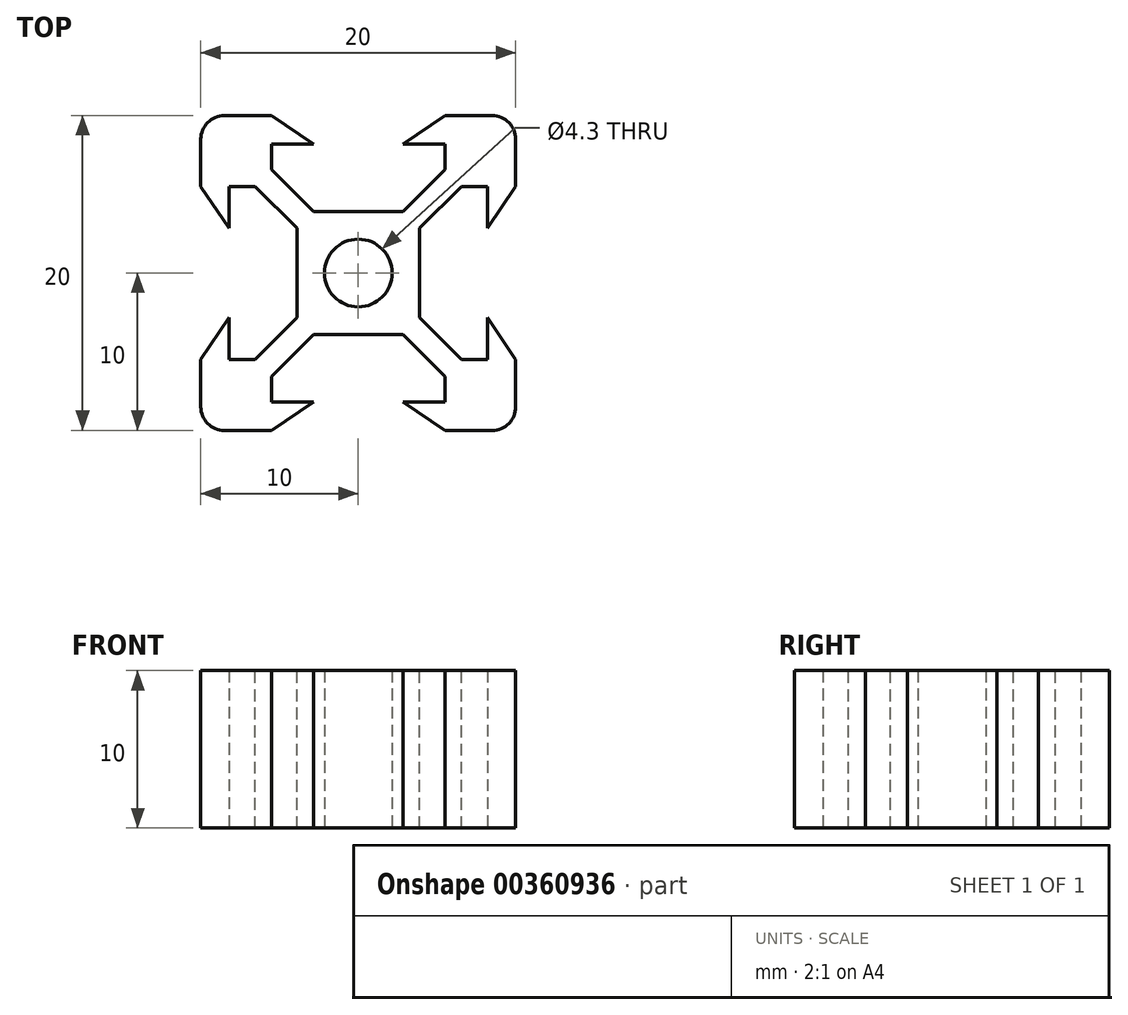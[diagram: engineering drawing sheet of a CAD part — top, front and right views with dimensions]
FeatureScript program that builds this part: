
annotation { "Feature Type Name" : "Feature", "Feature Type Description" : "" }
export const myFeature = defineFeature(function(context is Context, id is Id, definition is map)
    precondition{}
    {
        {
            var Q0;
            Q0=qCreatedBy(makeId("Top.planeOp"),FACE);
            var sketch = newSketch(context, id + "F0", { "sketchPlane" : qUnion([Q0])});
            skPoint(sketch, "E0.middle", {"position": v(0, 0) * mm});
            skPoint(sketch, "E1.visualSharp", {"position": v(-10, 10) * mm});
            skArc(sketch, "E1.filletArc", {"start": v(-8.5, 10) * mm, "mid": v(-9.56, 9.56) * mm, "end": v(-10, 8.5) * mm});
            skPoint(sketch, "E2.visualSharp", {"position": v(10, 10) * mm});
            skArc(sketch, "E2.filletArc", {"start": v(10, 8.5) * mm, "mid": v(9.56, 9.56) * mm, "end": v(8.5, 10) * mm});
            skPoint(sketch, "E3.visualSharp", {"position": v(10, -10) * mm});
            skArc(sketch, "E3.filletArc", {"start": v(8.5, -10) * mm, "mid": v(9.56, -9.56) * mm, "end": v(10, -8.5) * mm});
            skPoint(sketch, "E4.visualSharp", {"position": v(-10, -10) * mm});
            skArc(sketch, "E4.filletArc", {"start": v(-10, -8.5) * mm, "mid": v(-9.56, -9.56) * mm, "end": v(-8.5, -10) * mm});
            skLineSegment(sketch, "E5", {"start": v(-10, 5.5) * mm, "end": v(-8.2, 2.84) * mm});
            skLineSegment(sketch, "E6", {"start": v(-8.2, -2.84) * mm, "end": v(-10, -5.5) * mm});
            skLineSegment(sketch, "E7.1.0", {"start": v(-5.5, -10) * mm, "end": v(-2.84, -8.2) * mm});
            skLineSegment(sketch, "E7.1.2", {"start": v(2.84, -8.2) * mm, "end": v(5.5, -10) * mm});
            skLineSegment(sketch, "E7.2.0", {"start": v(10, -5.5) * mm, "end": v(8.2, -2.84) * mm});
            skLineSegment(sketch, "E7.2.2", {"start": v(8.2, 2.84) * mm, "end": v(10, 5.5) * mm});
            skLineSegment(sketch, "E7.3.0", {"start": v(5.5, 10) * mm, "end": v(2.84, 8.2) * mm});
            skLineSegment(sketch, "E7.3.2", {"start": v(-2.84, 8.2) * mm, "end": v(-5.5, 10) * mm});
            skLineSegment(sketch, "E8", {"start": v(-10, 5.5) * mm, "end": v(-10, 8.5) * mm});
            skLineSegment(sketch, "E9", {"start": v(-8.5, 10) * mm, "end": v(-5.5, 10) * mm});
            skLineSegment(sketch, "E10", {"start": v(5.5, 10) * mm, "end": v(8.5, 10) * mm});
            skLineSegment(sketch, "E11", {"start": v(10, 8.5) * mm, "end": v(10, 5.5) * mm});
            skLineSegment(sketch, "E12", {"start": v(10, -5.5) * mm, "end": v(10, -8.5) * mm});
            skLineSegment(sketch, "E13", {"start": v(5.5, -10) * mm, "end": v(8.5, -10) * mm});
            skLineSegment(sketch, "E14", {"start": v(-5.5, -10) * mm, "end": v(-8.5, -10) * mm});
            skLineSegment(sketch, "E15", {"start": v(-10, -8.5) * mm, "end": v(-10, -5.5) * mm});
            skCircle(sketch, "E16", {"center": v(0, 0) * mm, "radius": 2.15 * mm});
            skLineSegment(sketch, "E17", {"start": v(-8.2, 2.84) * mm, "end": v(-8.2, -2.84) * mm});
            skLineSegment(sketch, "E18", {"start": v(-2.84, -8.2) * mm, "end": v(2.84, -8.2) * mm});
            skLineSegment(sketch, "E19", {"start": v(8.2, -2.84) * mm, "end": v(8.2, 2.84) * mm});
            skLineSegment(sketch, "E20", {"start": v(2.84, 8.2) * mm, "end": v(-2.84, 8.2) * mm});
            skSolve(sketch);
        }
        {
            var Q0;
            Q0=qSketchRegion(id+"F0",true);
            extrude(context, id + "F1", {"entities" : qUnion([Q0]), "depth" : 10 * mm});
        }
        {
            var Q0;
            Q0=makeQuery(id+"F1.opExtrude","CAP_FACE",FACE,{"disambiguationData":[OSD([sQuery(id+"F0.wireOp",EDGE,"E1.filletArc"),sQuery(id+"F0.wireOp",EDGE,"E2.filletArc"),sQuery(id+"F0.wireOp",EDGE,"E3.filletArc"),sQuery(id+"F0.wireOp",EDGE,"E4.filletArc"),sQuery(id+"F0.wireOp",EDGE,"E5"),sQuery(id+"F0.wireOp",EDGE,"E6"),sQuery(id+"F0.wireOp",EDGE,"E7.1.0"),sQuery(id+"F0.wireOp",EDGE,"E7.1.2"),sQuery(id+"F0.wireOp",EDGE,"E7.2.0"),sQuery(id+"F0.wireOp",EDGE,"E7.2.2"),sQuery(id+"F0.wireOp",EDGE,"E7.3.0"),sQuery(id+"F0.wireOp",EDGE,"E7.3.2"),sQuery(id+"F0.wireOp",EDGE,"E8"),sQuery(id+"F0.wireOp",EDGE,"E9"),sQuery(id+"F0.wireOp",EDGE,"E10"),sQuery(id+"F0.wireOp",EDGE,"E11"),sQuery(id+"F0.wireOp",EDGE,"E12"),sQuery(id+"F0.wireOp",EDGE,"E13"),sQuery(id+"F0.wireOp",EDGE,"E14"),sQuery(id+"F0.wireOp",EDGE,"E15"),sQuery(id+"F0.wireOp",EDGE,"E16"),sQuery(id+"F0.wireOp",EDGE,"E17"),sQuery(id+"F0.wireOp",EDGE,"E18"),sQuery(id+"F0.wireOp",EDGE,"E19"),sQuery(id+"F0.wireOp",EDGE,"E20")])],"isStart":false});
            var sketch = newSketch(context, id + "F2", { "sketchPlane" : qUnion([Q0])});
            skLineSegment(sketch, "E21", {"start": v(-8.2, 2.84) * mm, "end": v(-8.2, 5.5) * mm});
            skLineSegment(sketch, "E22", {"start": v(-8.2, 5.5) * mm, "end": v(-6.56, 5.5) * mm});
            skLineSegment(sketch, "E23", {"start": v(-6.56, 5.5) * mm, "end": v(-3.9, 2.84) * mm});
            skLineSegment(sketch, "E24", {"start": v(-8.2, -2.84) * mm, "end": v(-8.2, -5.5) * mm});
            skLineSegment(sketch, "E25", {"start": v(-8.2, -5.5) * mm, "end": v(-6.56, -5.5) * mm});
            skLineSegment(sketch, "E26", {"start": v(-6.56, -5.5) * mm, "end": v(-3.9, -2.84) * mm});
            skLineSegment(sketch, "E27", {"start": v(-3.9, -2.84) * mm, "end": v(-3.9, 2.84) * mm});
            skLineSegment(sketch, "E28", {"start": v(-8.2, 2.84) * mm, "end": v(-8.2, -2.84) * mm});
            skLineSegment(sketch, "E29.1.0", {"start": v(-2.84, -8.2) * mm, "end": v(2.84, -8.2) * mm});
            skLineSegment(sketch, "E29.1.1", {"start": v(-2.84, -8.2) * mm, "end": v(-5.5, -8.2) * mm});
            skLineSegment(sketch, "E29.1.2", {"start": v(-5.5, -8.2) * mm, "end": v(-5.5, -6.56) * mm});
            skLineSegment(sketch, "E29.1.3", {"start": v(5.5, -8.2) * mm, "end": v(5.5, -6.56) * mm});
            skLineSegment(sketch, "E29.1.4", {"start": v(2.84, -8.2) * mm, "end": v(5.5, -8.2) * mm});
            skLineSegment(sketch, "E29.1.5", {"start": v(2.84, -3.9) * mm, "end": v(-2.84, -3.9) * mm});
            skLineSegment(sketch, "E29.1.6", {"start": v(5.5, -6.56) * mm, "end": v(2.84, -3.9) * mm});
            skLineSegment(sketch, "E29.1.7", {"start": v(-5.5, -6.56) * mm, "end": v(-2.84, -3.9) * mm});
            skLineSegment(sketch, "E29.2.0", {"start": v(8.2, -2.84) * mm, "end": v(8.2, 2.84) * mm});
            skLineSegment(sketch, "E29.2.1", {"start": v(8.2, -2.84) * mm, "end": v(8.2, -5.5) * mm});
            skLineSegment(sketch, "E29.2.2", {"start": v(8.2, -5.5) * mm, "end": v(6.56, -5.5) * mm});
            skLineSegment(sketch, "E29.2.3", {"start": v(8.2, 5.5) * mm, "end": v(6.56, 5.5) * mm});
            skLineSegment(sketch, "E29.2.4", {"start": v(8.2, 2.84) * mm, "end": v(8.2, 5.5) * mm});
            skLineSegment(sketch, "E29.2.5", {"start": v(3.9, 2.84) * mm, "end": v(3.9, -2.84) * mm});
            skLineSegment(sketch, "E29.2.6", {"start": v(6.56, 5.5) * mm, "end": v(3.9, 2.84) * mm});
            skLineSegment(sketch, "E29.2.7", {"start": v(6.56, -5.5) * mm, "end": v(3.9, -2.84) * mm});
            skLineSegment(sketch, "E29.3.0", {"start": v(2.84, 8.2) * mm, "end": v(-2.84, 8.2) * mm});
            skLineSegment(sketch, "E29.3.1", {"start": v(2.84, 8.2) * mm, "end": v(5.5, 8.2) * mm});
            skLineSegment(sketch, "E29.3.2", {"start": v(5.5, 8.2) * mm, "end": v(5.5, 6.56) * mm});
            skLineSegment(sketch, "E29.3.3", {"start": v(-5.5, 8.2) * mm, "end": v(-5.5, 6.56) * mm});
            skLineSegment(sketch, "E29.3.4", {"start": v(-2.84, 8.2) * mm, "end": v(-5.5, 8.2) * mm});
            skLineSegment(sketch, "E29.3.5", {"start": v(-2.84, 3.9) * mm, "end": v(2.84, 3.9) * mm});
            skLineSegment(sketch, "E29.3.6", {"start": v(-5.5, 6.56) * mm, "end": v(-2.84, 3.9) * mm});
            skLineSegment(sketch, "E29.3.7", {"start": v(5.5, 6.56) * mm, "end": v(2.84, 3.9) * mm});
            skPoint(sketch, "E29.center", {"position": v(0, 0) * mm});
            skSolve(sketch);
        }
        {
            var Q0;
            Q0=qSketchRegion(id+"F2",true);
            extrude(context, id + "F3", {"entities" : qUnion([Q0]), "operationType" : NewBodyOperationType.REMOVE, "oppositeDirection" : true, "depth" : 10 * mm});
        }
    });
